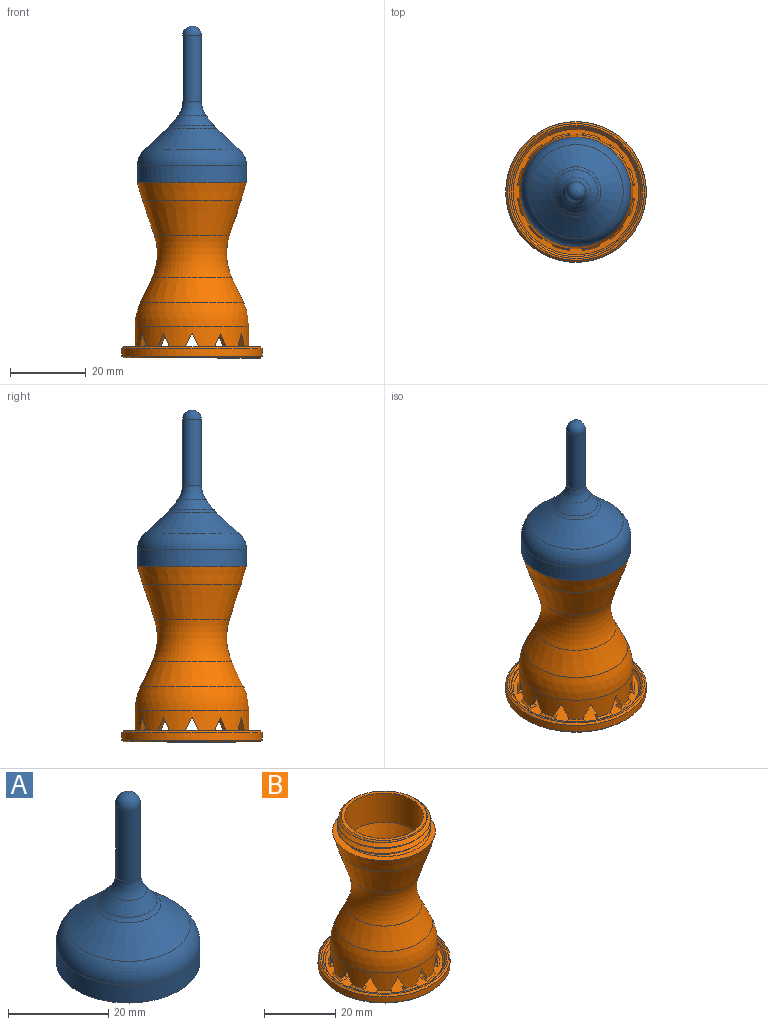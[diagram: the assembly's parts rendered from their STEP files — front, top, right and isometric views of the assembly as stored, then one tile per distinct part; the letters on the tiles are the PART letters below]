
ASSEMBLY  parts=2 mates=1
PART A: 19 faces, bbox 31.2x31.2x42.2 mm
  f0: cone r=14.4mm half-angle=48deg, axis (0,0,-1), area 471mm2, adj f14,f16
  f1: cylinder r=14.4mm len=28.8mm, axis (0,0,1), area 391.6mm2, adj f2,f16
  f2: plane 28.8x28.8mm, normal (0,0,-1), area 87.3mm2, adj f1,f5
  f3: cylinder r=2.5mm len=17.46mm, axis (0,0,-1), area 274.3mm2, adj f15,f17
  f4: cone r=6.13mm half-angle=37.5deg, axis (0,0,-1), area 100.9mm2, adj f14,f15
  f5: cone r=12.4mm half-angle=45deg, axis (0,0,-1), area 59.4mm2, adj f2,f10,f11,f13
  f6: plane 1x1mm, normal (0,0,-1), area 0.8mm2, adj f7
  f7: cylinder r=0.5mm len=1mm, axis (0,0,-1), area 2.1mm2, adj f6,f8
  f8: cone r=4.54mm half-angle=37.5deg, axis (0,0,-1), area 110.4mm2, adj f7,f9
  f9: cone r=13.06mm half-angle=48deg, axis (0,0,-1), area 520.2mm2, adj f8,f18
  f10: cylinder r=12.4mm len=24.8mm, axis (0,0,1), area 57.9mm2, adj f5,f11,f12,f13,f18
  f11: bspline ~30.95x26.8mm, area 224.4mm2, adj f5,f10,f12,f13
  f12: plane 2.32x1.22mm, normal (0.37,0.93,0), area 1.1mm2, adj f10,f11,f13,f18
  f13: bspline ~30.95x26.8mm, area 283.2mm2, adj f5,f10,f11,f12,f18
  f14: torus R=10.55mm, axis (0,0,-1), area 42.5mm2, adj f0,f4
  f15: torus R=8.5mm, axis (0,0,-1), area 72mm2, adj f3,f4
  f16: torus R=8.4mm, axis (0,0,-1), area 433.4mm2, adj f0,f1
  f17: sphere r=2.5mm, area 39.3mm2, adj f3
  f18: cone r=12.4mm half-angle=24deg, axis (0,0,-1), area 64.4mm2, adj f9,f10,f12,f13
PART B: 100 faces, bbox 37.9x37.9x53.4 mm
  f0: cone r=6.58mm half-angle=18.4deg, axis (0,0,1), area 583.1mm2, adj f16,f91
  f1: cylinder r=15mm len=30mm, axis (0,0,1), area 460.5mm2, adj f13,f18,f19,f20,f21,f22,f23,f24
  f2: cone r=8mm half-angle=18.4deg, axis (0,0,1), area 707.2mm2, adj f12,f99
  f3: cone r=15mm half-angle=25deg, axis (0,0,-1), area 549.2mm2, adj f12,f13
  f4: plane 33x33mm, normal (0,0,1), area 733.2mm2, adj f42,f43,f44,f45,f46,f47,f48,f49
  f5: cylinder r=17mm len=34mm, axis (0,0,1), area 53.4mm2, adj f11,f90
  f6: plane 36x36mm, normal (0,0,1), area 55.8mm2, adj f10,f11
  f7: cylinder r=18.5mm len=37mm, axis (0,0,1), area 232.5mm2, adj f9,f10
  f8: plane 36x36mm, normal (0,0,-1), area 1017.9mm2, adj f9
  f9: cone r=18.5mm half-angle=45deg, axis (0,0,1), area 81.1mm2, adj f7,f8
  f10: cone r=18mm half-angle=45deg, axis (0,0,-1), area 81.1mm2, adj f6,f7
  f11: cone r=17mm half-angle=45deg, axis (0,0,1), area 76.6mm2, adj f5,f6
  f12: torus R=24.12mm, axis (0,0,1), area 679.1mm2, adj f2,f3
  f13: sphere r=15mm, area 597.8mm2, adj f1,f3
  f14: cylinder r=13.5mm len=27mm, axis (0,0,1), area 402.2mm2, adj f17,f18,f19,f20,f21,f22,f23,f24
  f15: cone r=13.64mm half-angle=25deg, axis (0,0,-1), area 487.3mm2, adj f16,f17
  f16: torus R=24.12mm, axis (0,0,1), area 632.1mm2, adj f0,f15
  f17: sphere r=13.5mm, area 484.3mm2, adj f14,f15
  f18: plane 4.29x2.54mm, normal (0.77,0.45,-0.45), area 7.2mm2, adj f1,f14,f19,f44
  f19: plane 4.29x2.7mm, normal (-0.77,-0.45,-0.45), area 7.2mm2, adj f1,f14,f18,f87
  f20: plane 4.29x2.7mm, normal (0.45,0.77,-0.45), area 7.2mm2, adj f1,f14,f21,f48
  f21: plane 4.29x2.54mm, normal (-0.45,-0.77,-0.45), area 7.2mm2, adj f1,f14,f20,f43
  f22: plane 4.29x2.15mm, normal (0,0.89,-0.45), area 7.2mm2, adj f1,f14,f23,f52
  f23: plane 4.29x2.15mm, normal (0,-0.89,-0.45), area 7.2mm2, adj f1,f14,f22,f47
  f24: plane 4.29x2.54mm, normal (-0.45,0.77,-0.45), area 7.2mm2, adj f1,f14,f25,f56
  f25: plane 4.29x2.7mm, normal (0.45,-0.77,-0.45), area 7.2mm2, adj f1,f14,f24,f51
  f26: plane 4.29x2.7mm, normal (-0.77,0.45,-0.45), area 7.2mm2, adj f1,f14,f27,f60
  f27: plane 4.29x2.54mm, normal (0.77,-0.45,-0.45), area 7.2mm2, adj f1,f14,f26,f55
  f28: plane 4.29x2.15mm, normal (-0.89,0,-0.45), area 7.2mm2, adj f1,f14,f29,f64
  f29: plane 4.29x2.15mm, normal (0.89,0,-0.45), area 7.2mm2, adj f1,f14,f28,f59
  f30: plane 4.29x2.54mm, normal (-0.77,-0.45,-0.45), area 7.2mm2, adj f1,f14,f31,f68
  f31: plane 4.29x2.7mm, normal (0.77,0.45,-0.45), area 7.2mm2, adj f1,f14,f30,f63
  f32: plane 4.29x2.7mm, normal (-0.45,-0.77,-0.45), area 7.2mm2, adj f1,f14,f33,f72
  f33: plane 4.29x2.54mm, normal (0.45,0.77,-0.45), area 7.2mm2, adj f1,f14,f32,f67
  f34: plane 4.29x2.15mm, normal (0,-0.89,-0.45), area 7.2mm2, adj f1,f14,f35,f76
  f35: plane 4.29x2.15mm, normal (0,0.89,-0.45), area 7.2mm2, adj f1,f14,f34,f71
  f36: plane 4.29x2.54mm, normal (0.45,-0.77,-0.45), area 7.2mm2, adj f1,f14,f37,f80
  f37: plane 4.29x2.7mm, normal (-0.45,0.77,-0.45), area 7.2mm2, adj f1,f14,f36,f75
  f38: plane 4.29x2.7mm, normal (0.77,-0.45,-0.45), area 7.2mm2, adj f1,f14,f39,f84
  f39: plane 4.29x2.54mm, normal (-0.77,0.45,-0.45), area 7.2mm2, adj f1,f14,f38,f79
  f40: plane 4.29x2.15mm, normal (-0.89,0,-0.45), area 7.2mm2, adj f1,f14,f41,f83
  f41: plane 4.29x2.15mm, normal (0.89,0,-0.45), area 7.2mm2, adj f1,f14,f40,f88
  f42: cone r=15mm half-angle=45deg, axis (0,0,-1), area 3mm2, adj f1,f4,f43,f44
  f43: plane 2.19x1.37mm, normal (-0.43,-0.74,0.53), area 1.6mm2, adj f1,f4,f14,f21,f42,f45
  f44: plane 2.19x1.37mm, normal (0.74,0.43,0.53), area 1.6mm2, adj f1,f4,f14,f18,f42,f45
  f45: cone r=13.5mm half-angle=45deg, axis (0,0,1), area 2.3mm2, adj f4,f14,f43,f44
  f46: cone r=15mm half-angle=45deg, axis (0,0,-1), area 3mm2, adj f1,f4,f47,f48
  f47: plane 2.52x0.73mm, normal (0,-0.85,0.53), area 1.6mm2, adj f1,f4,f14,f23,f46,f49
  f48: plane 2.19x1.43mm, normal (0.43,0.74,0.53), area 1.6mm2, adj f1,f4,f14,f20,f46,f49
  f49: cone r=13.5mm half-angle=45deg, axis (0,0,1), area 2.3mm2, adj f4,f14,f47,f48
  f50: cone r=15mm half-angle=45deg, axis (0,0,-1), area 3mm2, adj f1,f4,f51,f52
  f51: plane 2.19x1.43mm, normal (0.43,-0.74,0.53), area 1.6mm2, adj f1,f4,f14,f25,f50,f53
  f52: plane 2.52x0.73mm, normal (0,0.85,0.53), area 1.6mm2, adj f1,f4,f14,f22,f50,f53
  f53: cone r=13.5mm half-angle=45deg, axis (0,0,1), area 2.3mm2, adj f4,f14,f51,f52
  f54: cone r=15mm half-angle=45deg, axis (0,0,-1), area 3mm2, adj f1,f4,f55,f56
  f55: plane 2.19x1.37mm, normal (0.74,-0.43,0.53), area 1.6mm2, adj f1,f4,f14,f27,f54,f57
  f56: plane 2.19x1.37mm, normal (-0.43,0.74,0.53), area 1.6mm2, adj f1,f4,f14,f24,f54,f57
  f57: cone r=13.5mm half-angle=45deg, axis (0,0,1), area 2.3mm2, adj f4,f14,f55,f56
  f58: cone r=15mm half-angle=45deg, axis (0,0,-1), area 3mm2, adj f1,f4,f59,f60
  f59: plane 2.52x0.73mm, normal (0.85,0,0.53), area 1.6mm2, adj f1,f4,f14,f29,f58,f61
  f60: plane 2.19x1.43mm, normal (-0.74,0.43,0.53), area 1.6mm2, adj f1,f4,f14,f26,f58,f61
  f61: cone r=13.5mm half-angle=45deg, axis (0,0,1), area 2.3mm2, adj f4,f14,f59,f60
  f62: cone r=15mm half-angle=45deg, axis (0,0,-1), area 3mm2, adj f1,f4,f63,f64
  f63: plane 2.19x1.43mm, normal (0.74,0.43,0.53), area 1.6mm2, adj f1,f4,f14,f31,f62,f65
  f64: plane 2.52x0.73mm, normal (-0.85,0,0.53), area 1.6mm2, adj f1,f4,f14,f28,f62,f65
  f65: cone r=13.5mm half-angle=45deg, axis (0,0,1), area 2.3mm2, adj f4,f14,f63,f64
  f66: cone r=15mm half-angle=45deg, axis (0,0,-1), area 3mm2, adj f1,f4,f67,f68
  f67: plane 2.19x1.37mm, normal (0.43,0.74,0.53), area 1.6mm2, adj f1,f4,f14,f33,f66,f69
  f68: plane 2.19x1.37mm, normal (-0.74,-0.43,0.53), area 1.6mm2, adj f1,f4,f14,f30,f66,f69
  f69: cone r=13.5mm half-angle=45deg, axis (0,0,1), area 2.3mm2, adj f4,f14,f67,f68
  f70: cone r=15mm half-angle=45deg, axis (0,0,-1), area 3mm2, adj f1,f4,f71,f72
  f71: plane 2.52x0.73mm, normal (0,0.85,0.53), area 1.6mm2, adj f1,f4,f14,f35,f70,f73
  f72: plane 2.19x1.43mm, normal (-0.43,-0.74,0.53), area 1.6mm2, adj f1,f4,f14,f32,f70,f73
  f73: cone r=13.5mm half-angle=45deg, axis (0,0,1), area 2.3mm2, adj f4,f14,f71,f72
  f74: cone r=15mm half-angle=45deg, axis (0,0,-1), area 3mm2, adj f1,f4,f75,f76
  f75: plane 2.19x1.43mm, normal (-0.43,0.74,0.53), area 1.6mm2, adj f1,f4,f14,f37,f74,f77
  f76: plane 2.52x0.73mm, normal (0,-0.85,0.53), area 1.6mm2, adj f1,f4,f14,f34,f74,f77
  f77: cone r=13.5mm half-angle=45deg, axis (0,0,1), area 2.3mm2, adj f4,f14,f75,f76
  f78: cone r=15mm half-angle=45deg, axis (0,0,-1), area 3mm2, adj f1,f4,f79,f80
  f79: plane 2.19x1.37mm, normal (-0.74,0.43,0.53), area 1.6mm2, adj f1,f4,f14,f39,f78,f81
  f80: plane 2.19x1.37mm, normal (0.43,-0.74,0.53), area 1.6mm2, adj f1,f4,f14,f36,f78,f81
  f81: cone r=13.5mm half-angle=45deg, axis (0,0,1), area 2.3mm2, adj f4,f14,f79,f80
  f82: cone r=15mm half-angle=45deg, axis (0,0,-1), area 3mm2, adj f1,f4,f83,f84
  f83: plane 2.52x0.73mm, normal (-0.85,0,0.53), area 1.6mm2, adj f1,f4,f14,f40,f82,f85
  f84: plane 2.19x1.43mm, normal (0.74,-0.43,0.53), area 1.6mm2, adj f1,f4,f14,f38,f82,f85
  f85: cone r=13.5mm half-angle=45deg, axis (0,0,1), area 2.3mm2, adj f4,f14,f83,f84
  f86: cone r=15mm half-angle=45deg, axis (0,0,-1), area 3mm2, adj f1,f4,f87,f88
  f87: plane 2.19x1.43mm, normal (-0.74,-0.43,0.53), area 1.6mm2, adj f1,f4,f14,f19,f86,f89
  f88: plane 2.52x0.73mm, normal (0.85,0,0.53), area 1.6mm2, adj f1,f4,f14,f41,f86,f89
  f89: cone r=13.5mm half-angle=45deg, axis (0,0,1), area 2.3mm2, adj f4,f14,f87,f88
  f90: cone r=16.5mm half-angle=45deg, axis (0,0,1), area 74.4mm2, adj f4,f5
  f91: plane 22.84x22.84mm, normal (0,0,-1), area 29.5mm2, adj f0,f97
  f92: cone r=13mm half-angle=45deg, axis (0,0,-1), area 55.1mm2, adj f93,f94,f95,f96
  f93: bspline ~30.02x26mm, area 259.4mm2, adj f92,f94,f95,f98
  f94: bspline ~30.02x26mm, area 259.4mm2, adj f92,f93,f95,f98
  f95: cylinder r=13mm len=26mm, axis (0,0,1), area 1.7mm2, adj f92,f93,f94,f98
  f96: plane 24x24mm, normal (0,0,1), area 72.3mm2, adj f92,f97
  f97: cylinder r=11mm len=22mm, axis (0,0,1), area 691.2mm2, adj f91,f96
  f98: plane 29.69x29.69mm, normal (0,0,1), area 160.1mm2, adj f93,f94,f95,f99
  f99: cone r=13mm half-angle=16.3deg, axis (0,0,1), area 430.4mm2, adj f2,f98
PLACE A rot(axis=(0,0,1),180deg) t=(19.83,3.81,149.02)mm
PLACE B rot(axis=(0,0,1),180deg) t=(69.08,3.81,104.31)mm
MATE revolute B.f5 <-> A.f0  axis (0,0,-1) through (19.83,3.81,102.81)mm
